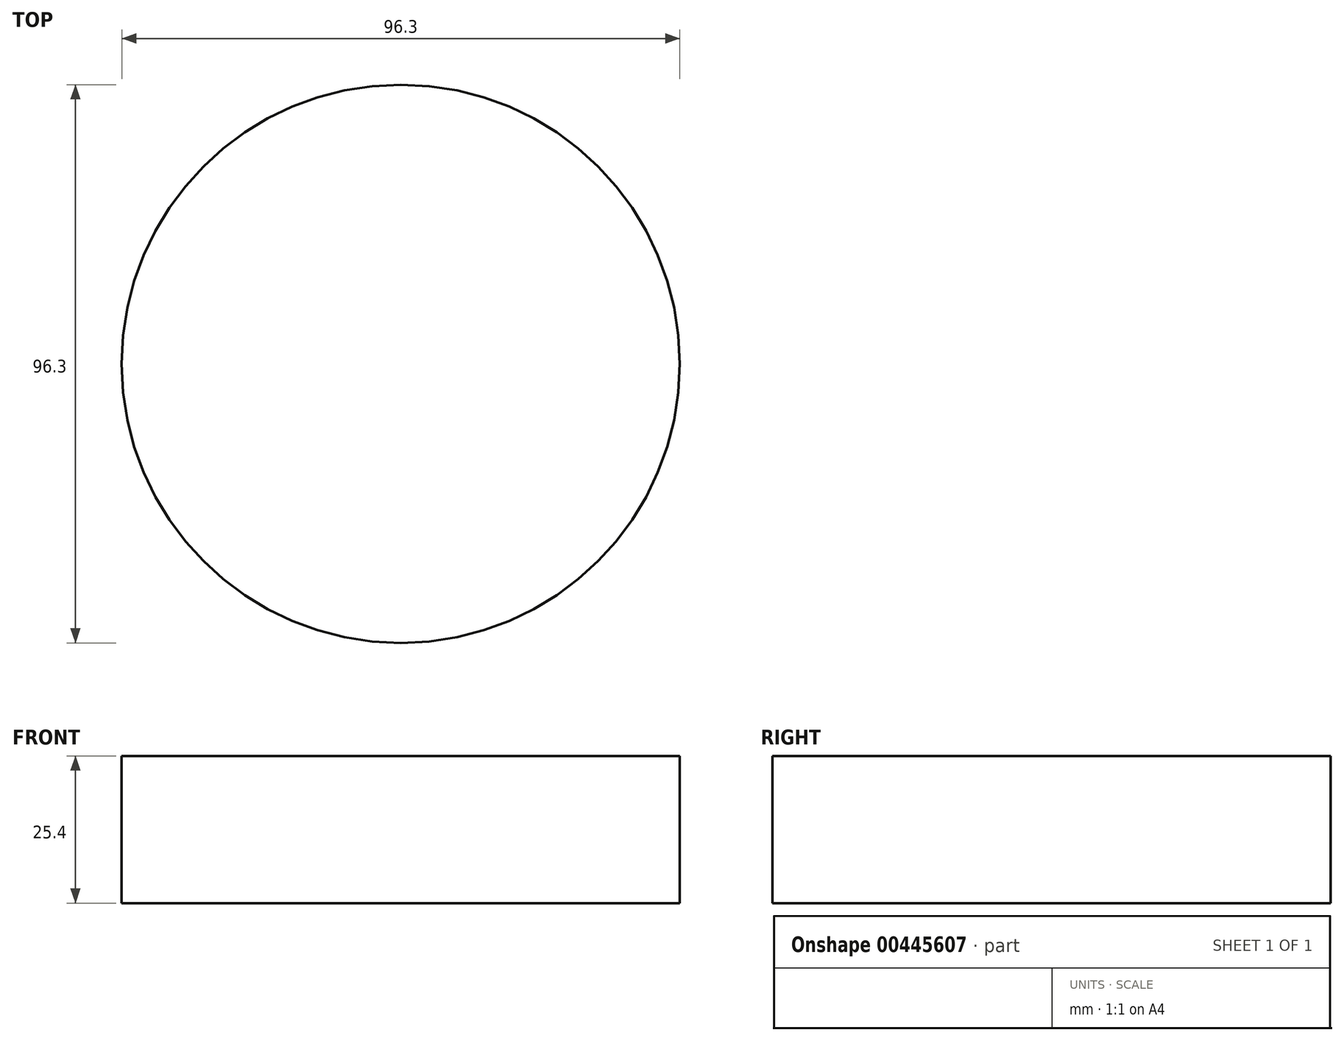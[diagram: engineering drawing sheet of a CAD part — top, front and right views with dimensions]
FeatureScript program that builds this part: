
annotation { "Feature Type Name" : "Feature", "Feature Type Description" : "" }
export const myFeature = defineFeature(function(context is Context, id is Id, definition is map)
    precondition{}
    {
        {
            var Q0;
            Q0=qCreatedBy(makeId("Top.planeOp"),FACE);
            var sketch = newSketch(context, id + "F0", { "sketchPlane" : qUnion([Q0])});
            skCircle(sketch, "E0", {"center": v(0, 0) * mm, "radius": 48.15 * mm});
            skSolve(sketch);
        }
        {
            var Q0;
            Q0 = qSketchRegion(id + "F0", true);
            extrude(context, id + "F1", {"entities" : qUnion([Q0]), "depth" : 25.4 * mm});
        }
    });
